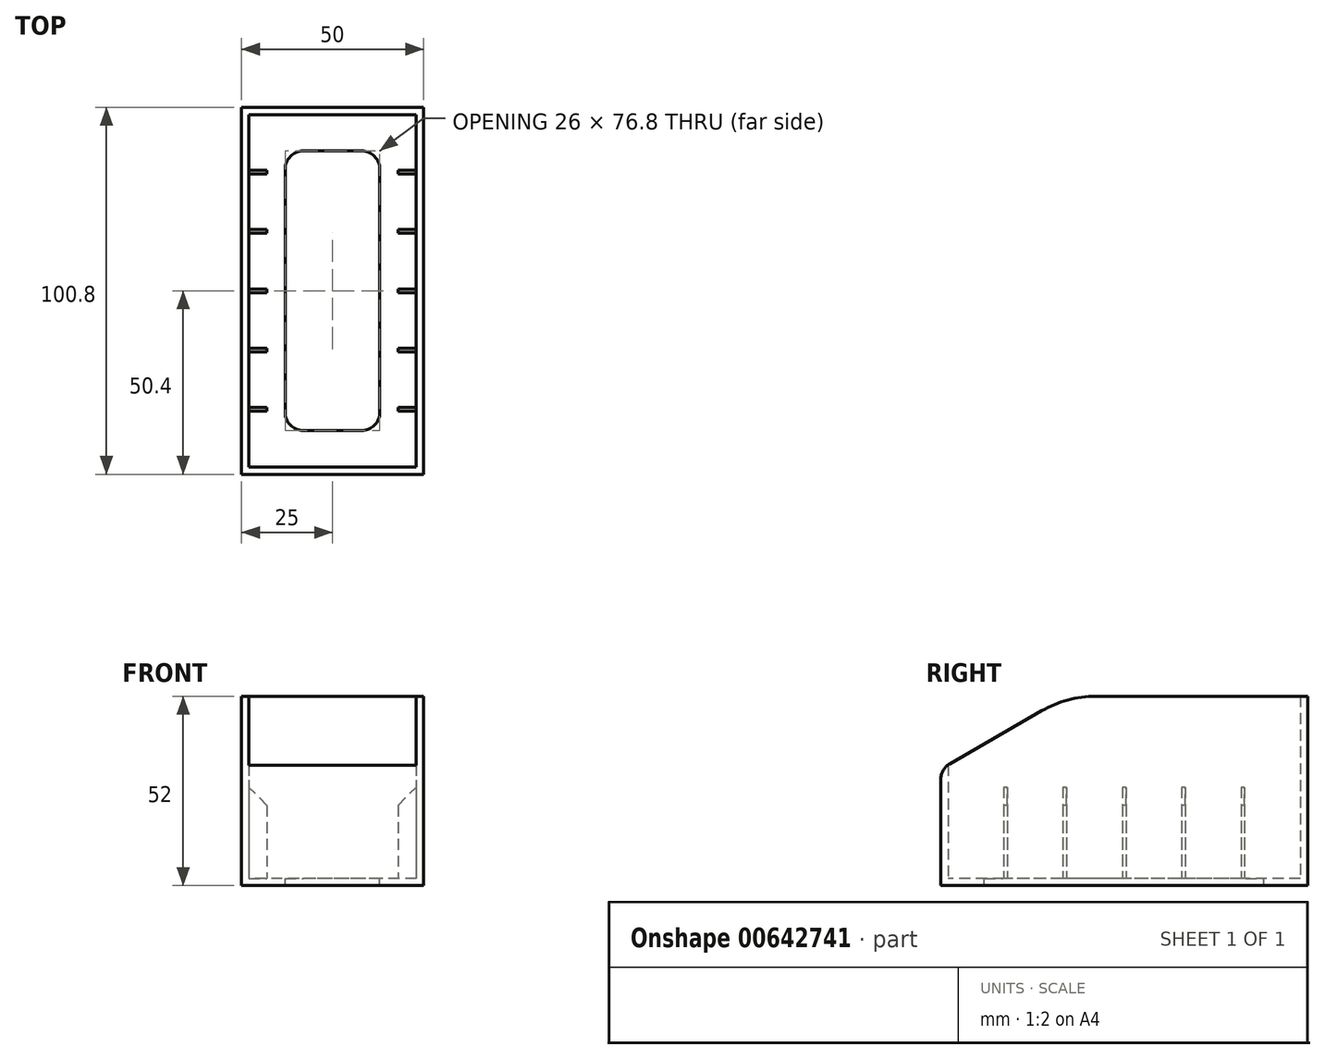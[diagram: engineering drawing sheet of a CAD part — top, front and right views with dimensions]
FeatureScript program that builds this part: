
annotation { "Feature Type Name" : "Feature", "Feature Type Description" : "" }
export const myFeature = defineFeature(function(context is Context, id is Id, definition is map)
    precondition{}
    {
        {
            var Q0;
            Q0=qCreatedBy(makeId("Top.planeOp"),FACE);
            var sketch = newSketch(context, id + "F0", { "sketchPlane" : qUnion([Q0])});
            skLineSegment(sketch, "E0.bottom", {"start": v(23, 48.4) * mm, "end": v(-23, 48.4) * mm});
            skLineSegment(sketch, "E0.top", {"start": v(23, -48.4) * mm, "end": v(-23, -48.4) * mm});
            skLineSegment(sketch, "E0.left", {"start": v(23, 48.4) * mm, "end": v(23, -48.4) * mm});
            skLineSegment(sketch, "E0.right", {"start": v(-23, 48.4) * mm, "end": v(-23, -48.4) * mm});
            skPoint(sketch, "E0.middle", {"position": v(0, 0) * mm});
            skLineSegment(sketch, "E1.bottom", {"start": v(25, 50.4) * mm, "end": v(-25, 50.4) * mm});
            skLineSegment(sketch, "E1.top", {"start": v(25, -50.4) * mm, "end": v(-25, -50.4) * mm});
            skLineSegment(sketch, "E1.left", {"start": v(25, 50.4) * mm, "end": v(25, -50.4) * mm});
            skLineSegment(sketch, "E1.right", {"start": v(-25, 50.4) * mm, "end": v(-25, -50.4) * mm});
            skSolve(sketch);
        }
        {
            var Q0;
            Q0 = qSketchRegion(id + "F0", true);
            extrude(context, id + "F1", {"entities" : qUnion([Q0]), "depth" : 50 * mm, "offsetDistance" : 25 * mm});
        }
        {
            var Q0;
            Q0=qCreatedBy(makeId("Top.planeOp"),FACE);
            var sketch = newSketch(context, id + "F2", { "sketchPlane" : qUnion([Q0])});
            skLineSegment(sketch, "E2.0", {"start": v(-25, 50.4) * mm, "end": v(-25, -50.4) * mm});
            skLineSegment(sketch, "E3.0", {"start": v(25, -50.4) * mm, "end": v(-25, -50.4) * mm});
            skLineSegment(sketch, "E4.0", {"start": v(25, 50.4) * mm, "end": v(25, -50.4) * mm});
            skLineSegment(sketch, "E5.0", {"start": v(25, 50.4) * mm, "end": v(-25, 50.4) * mm});
            skLineSegment(sketch, "E6.bottom", {"start": v(13, 38.4) * mm, "end": v(-13, 38.4) * mm});
            skLineSegment(sketch, "E6.top", {"start": v(13, -38.4) * mm, "end": v(-13, -38.4) * mm});
            skLineSegment(sketch, "E6.left", {"start": v(13, 38.4) * mm, "end": v(13, -38.4) * mm});
            skLineSegment(sketch, "E6.right", {"start": v(-13, 38.4) * mm, "end": v(-13, -38.4) * mm});
            skPoint(sketch, "E6.middle", {"position": v(0, 0) * mm});
            skSolve(sketch);
        }
        {
            var Q0;
            Q0=makeQuery(id+"F2.imprint","IMPRINT",FACE,{"disambiguationData":[TD([[makeQuery(id+"F2.imprint","IMPRINT",EDGE,{"derivedFrom":sQuery(id+"F2.wireOp",EDGE,"E2.0")}),1.0]])]});
            extrude(context, id + "F3", {"entities" : qUnion([Q0]), "operationType" : NewBodyOperationType.ADD, "oppositeDirection" : true, "depth" : 2 * mm, "offsetDistance" : 25 * mm});
        }
        {
            var Q0;
            Q0=makeQuery(id+"F1.opExtrude","CAP_EDGE",EDGE,{"disambiguationData":[OSD([sQuery(id+"F0.wireOp",EDGE,"E1.top")])],"isStart":false});
            chamfer(context, id + "F4", {"entities" : qUnion([Q0]), "chamferType" : ChamferType.OFFSET_ANGLE, "width" : 20 * mm, "oppositeDirection" : false, "angle" : 60 * degree, "tangentPropagation" : true});
        }
        {
            var Q0;
            {var subQ0=sQuery(id+"F0.wireOp",EDGE,"E1.top");Q0=makeQuery(id+"F4.opChamfer","BLEND_EDGE",EDGE,{"disambiguationData":[OD(1.0)],"blendedFrom":[makeQuery(id+"F1.opExtrude","CAP_EDGE",EDGE,{"disambiguationData":[OSD([subQ0])],"isStart":false}),makeQuery(id+"F1.opExtrude","CAP_FACE",FACE,{"disambiguationData":[OSD([sQuery(id+"F0.wireOp",EDGE,"E0.bottom"),sQuery(id+"F0.wireOp",EDGE,"E0.top"),sQuery(id+"F0.wireOp",EDGE,"E0.left"),sQuery(id+"F0.wireOp",EDGE,"E0.right"),sQuery(id+"F0.wireOp",EDGE,"E1.bottom"),subQ0,sQuery(id+"F0.wireOp",EDGE,"E1.left"),sQuery(id+"F0.wireOp",EDGE,"E1.right")])],"isStart":false})],"blendedInto":[makeQuery(id+"F1.opExtrude","CAP_FACE",FACE,{"disambiguationData":[OSD([sQuery(id+"F0.wireOp",EDGE,"E0.bottom"),sQuery(id+"F0.wireOp",EDGE,"E0.top"),sQuery(id+"F0.wireOp",EDGE,"E0.left"),sQuery(id+"F0.wireOp",EDGE,"E0.right"),sQuery(id+"F0.wireOp",EDGE,"E1.bottom"),subQ0,sQuery(id+"F0.wireOp",EDGE,"E1.left"),sQuery(id+"F0.wireOp",EDGE,"E1.right")])],"isStart":false})]});}
            var Q1;
            {var subQ0=sQuery(id+"F0.wireOp",EDGE,"E1.top");Q1=makeQuery(id+"F4.opChamfer","BLEND_EDGE",EDGE,{"disambiguationData":[OD(0.0)],"blendedFrom":[makeQuery(id+"F1.opExtrude","CAP_EDGE",EDGE,{"disambiguationData":[OSD([subQ0])],"isStart":false}),makeQuery(id+"F1.opExtrude","CAP_FACE",FACE,{"disambiguationData":[OSD([sQuery(id+"F0.wireOp",EDGE,"E0.bottom"),sQuery(id+"F0.wireOp",EDGE,"E0.top"),sQuery(id+"F0.wireOp",EDGE,"E0.left"),sQuery(id+"F0.wireOp",EDGE,"E0.right"),sQuery(id+"F0.wireOp",EDGE,"E1.bottom"),subQ0,sQuery(id+"F0.wireOp",EDGE,"E1.left"),sQuery(id+"F0.wireOp",EDGE,"E1.right")])],"isStart":false})],"blendedInto":[makeQuery(id+"F1.opExtrude","CAP_FACE",FACE,{"disambiguationData":[OSD([sQuery(id+"F0.wireOp",EDGE,"E0.bottom"),sQuery(id+"F0.wireOp",EDGE,"E0.top"),sQuery(id+"F0.wireOp",EDGE,"E0.left"),sQuery(id+"F0.wireOp",EDGE,"E0.right"),sQuery(id+"F0.wireOp",EDGE,"E1.bottom"),subQ0,sQuery(id+"F0.wireOp",EDGE,"E1.left"),sQuery(id+"F0.wireOp",EDGE,"E1.right")])],"isStart":false})]});}
            fillet(context, id + "F5", {"entities" : qUnion([Q0, Q1]), "radius" : 30 * mm, "tangentPropagation" : true, "allowEdgeOverflow" : false});
        }
        {
            var Q0;
            {var subQ0=sQuery(id+"F0.wireOp",EDGE,"E1.top");Q0=makeQuery(id+"F4.opChamfer","BLEND_EDGE",EDGE,{"blendedFrom":[makeQuery(id+"F1.opExtrude","CAP_EDGE",EDGE,{"disambiguationData":[OSD([subQ0])],"isStart":false}),makeQuery(id+"F3.boolean.opBoolean","MERGE",FACE,{"derivedFrom":[makeQuery(id+"F1.opExtrude","SWEPT_FACE",FACE,{"disambiguationData":[OSD([subQ0])]}),makeQuery(id+"F3.opExtrude","SWEPT_FACE",FACE,{"disambiguationData":[OSD([sQuery(id+"F2.wireOp",EDGE,"E3.0")])]})]})],"blendedInto":[makeQuery(id+"F3.boolean.opBoolean","MERGE",FACE,{"derivedFrom":[makeQuery(id+"F1.opExtrude","SWEPT_FACE",FACE,{"disambiguationData":[OSD([subQ0])]}),makeQuery(id+"F3.opExtrude","SWEPT_FACE",FACE,{"disambiguationData":[OSD([sQuery(id+"F2.wireOp",EDGE,"E3.0")])]})]})]});}
            fillet(context, id + "F6", {"entities" : qUnion([Q0]), "radius" : 5 * mm, "tangentPropagation" : true, "allowEdgeOverflow" : false});
        }
        {
            var Q0;
            Q0=makeQuery(id+"F3.opExtrude","SWEPT_EDGE",EDGE,{"disambiguationData":[OSD([sQuery(id+"F2.wireOp",EDGE,"E6.bottom"),sQuery(id+"F2.wireOp",EDGE,"E6.left")])]});
            var Q1;
            Q1=makeQuery(id+"F3.opExtrude","SWEPT_EDGE",EDGE,{"disambiguationData":[OSD([sQuery(id+"F2.wireOp",EDGE,"E6.bottom"),sQuery(id+"F2.wireOp",EDGE,"E6.right")])]});
            var Q2;
            Q2=makeQuery(id+"F3.opExtrude","SWEPT_EDGE",EDGE,{"disambiguationData":[OSD([sQuery(id+"F2.wireOp",EDGE,"E6.top"),sQuery(id+"F2.wireOp",EDGE,"E6.left")])]});
            var Q3;
            Q3=makeQuery(id+"F3.opExtrude","SWEPT_EDGE",EDGE,{"disambiguationData":[OSD([sQuery(id+"F2.wireOp",EDGE,"E6.top"),sQuery(id+"F2.wireOp",EDGE,"E6.right")])]});
            fillet(context, id + "F7", {"entities" : qUnion([Q0, Q1, Q2, Q3]), "radius" : 5 * mm, "tangentPropagation" : true, "allowEdgeOverflow" : false});
        }
        {
            var Q0;
            Q0=makeQuery(id+"F3.opExtrude","CAP_FACE",FACE,{"disambiguationData":[OSD([sQuery(id+"F2.wireOp",EDGE,"E2.0"),sQuery(id+"F2.wireOp",EDGE,"E3.0"),sQuery(id+"F2.wireOp",EDGE,"E4.0"),sQuery(id+"F2.wireOp",EDGE,"E5.0"),sQuery(id+"F2.wireOp",EDGE,"E6.bottom"),sQuery(id+"F2.wireOp",EDGE,"E6.top"),sQuery(id+"F2.wireOp",EDGE,"E6.left"),sQuery(id+"F2.wireOp",EDGE,"E6.right")])],"isStart":true});
            var sketch = newSketch(context, id + "F8", { "sketchPlane" : qUnion([Q0])});
            skLineSegment(sketch, "E7.bottom", {"start": v(-23, 33.1) * mm, "end": v(-18, 33.1) * mm});
            skLineSegment(sketch, "E7.top", {"start": v(-23, 32.1) * mm, "end": v(-18, 32.1) * mm});
            skLineSegment(sketch, "E7.left", {"start": v(-23, 33.1) * mm, "end": v(-23, 32.1) * mm});
            skLineSegment(sketch, "E7.right", {"start": v(-18, 33.1) * mm, "end": v(-18, 32.1) * mm});
            skLineSegment(sketch, "E8.bottom", {"start": v(-23, 16.8) * mm, "end": v(-18, 16.8) * mm});
            skLineSegment(sketch, "E8.top", {"start": v(-23, 15.8) * mm, "end": v(-18, 15.8) * mm});
            skLineSegment(sketch, "E8.left", {"start": v(-23, 16.8) * mm, "end": v(-23, 15.8) * mm});
            skLineSegment(sketch, "E8.right", {"start": v(-18, 16.8) * mm, "end": v(-18, 15.8) * mm});
            skLineSegment(sketch, "E9.bottom", {"start": v(-23, 0.5) * mm, "end": v(-18, 0.5) * mm});
            skLineSegment(sketch, "E9.top", {"start": v(-23, -0.5) * mm, "end": v(-18, -0.5) * mm});
            skLineSegment(sketch, "E9.left", {"start": v(-23, 0.5) * mm, "end": v(-23, -0.5) * mm});
            skLineSegment(sketch, "E9.right", {"start": v(-18, 0.5) * mm, "end": v(-18, -0.5) * mm});
            skLineSegment(sketch, "E10.bottom", {"start": v(-23, -15.8) * mm, "end": v(-18, -15.8) * mm});
            skLineSegment(sketch, "E10.top", {"start": v(-23, -16.8) * mm, "end": v(-18, -16.8) * mm});
            skLineSegment(sketch, "E10.left", {"start": v(-23, -15.8) * mm, "end": v(-23, -16.8) * mm});
            skLineSegment(sketch, "E10.right", {"start": v(-18, -15.8) * mm, "end": v(-18, -16.8) * mm});
            skLineSegment(sketch, "E11.bottom", {"start": v(-23, -32.1) * mm, "end": v(-18, -32.1) * mm});
            skLineSegment(sketch, "E11.top", {"start": v(-23, -33.1) * mm, "end": v(-18, -33.1) * mm});
            skLineSegment(sketch, "E11.left", {"start": v(-23, -32.1) * mm, "end": v(-23, -33.1) * mm});
            skLineSegment(sketch, "E11.right", {"start": v(-18, -32.1) * mm, "end": v(-18, -33.1) * mm});
            skLineSegment(sketch, "E12.MirrorCS", {"start": v(18, 33.1) * mm, "end": v(18, 32.1) * mm});
            skLineSegment(sketch, "E13.MirrorCS", {"start": v(18, -32.1) * mm, "end": v(18, -33.1) * mm});
            skLineSegment(sketch, "E14.MirrorCS", {"start": v(18, -15.8) * mm, "end": v(18, -16.8) * mm});
            skLineSegment(sketch, "E15.MirrorCS", {"start": v(23, 33.1) * mm, "end": v(23, 32.1) * mm});
            skLineSegment(sketch, "E16.MirrorCS", {"start": v(23, 16.8) * mm, "end": v(23, 15.8) * mm});
            skLineSegment(sketch, "E17.MirrorCS", {"start": v(23, -15.8) * mm, "end": v(23, -16.8) * mm});
            skLineSegment(sketch, "E18.MirrorCS", {"start": v(23, -32.1) * mm, "end": v(23, -33.1) * mm});
            skLineSegment(sketch, "E19.MirrorCS", {"start": v(23, 0.5) * mm, "end": v(23, -0.5) * mm});
            skLineSegment(sketch, "E20.MirrorCS", {"start": v(18, 0.5) * mm, "end": v(18, -0.5) * mm});
            skLineSegment(sketch, "E21.MirrorCS", {"start": v(18, 16.8) * mm, "end": v(18, 15.8) * mm});
            skLineSegment(sketch, "E22.MirrorCS", {"start": v(23, 16.8) * mm, "end": v(18, 16.8) * mm});
            skLineSegment(sketch, "E23.MirrorCS", {"start": v(23, 33.1) * mm, "end": v(18, 33.1) * mm});
            skLineSegment(sketch, "E24.MirrorCS", {"start": v(23, 32.1) * mm, "end": v(18, 32.1) * mm});
            skLineSegment(sketch, "E25.MirrorCS", {"start": v(23, 15.8) * mm, "end": v(18, 15.8) * mm});
            skLineSegment(sketch, "E26.MirrorCS", {"start": v(23, -16.8) * mm, "end": v(18, -16.8) * mm});
            skLineSegment(sketch, "E27.MirrorCS", {"start": v(23, -33.1) * mm, "end": v(18, -33.1) * mm});
            skLineSegment(sketch, "E28.MirrorCS", {"start": v(23, -32.1) * mm, "end": v(18, -32.1) * mm});
            skLineSegment(sketch, "E29.MirrorCS", {"start": v(23, -15.8) * mm, "end": v(18, -15.8) * mm});
            skLineSegment(sketch, "E30.MirrorCS", {"start": v(23, 0.5) * mm, "end": v(18, 0.5) * mm});
            skLineSegment(sketch, "E31.MirrorCS", {"start": v(23, -0.5) * mm, "end": v(18, -0.5) * mm});
            skSolve(sketch);
        }
        {
            var Q0;
            Q0=makeQuery(id+"F8.imprint","IMPRINT",FACE,{"disambiguationData":[TD([[makeQuery(id+"F8.imprint","IMPRINT",EDGE,{"derivedFrom":sQuery(id+"F8.wireOp",EDGE,"E7.bottom")}),-1.0]])]});
            var Q1;
            Q1=makeQuery(id+"F8.imprint","IMPRINT",FACE,{"disambiguationData":[TD([[makeQuery(id+"F8.imprint","IMPRINT",EDGE,{"derivedFrom":sQuery(id+"F8.wireOp",EDGE,"E8.bottom")}),-1.0]])]});
            var Q2;
            Q2=makeQuery(id+"F8.imprint","IMPRINT",FACE,{"disambiguationData":[TD([[makeQuery(id+"F8.imprint","IMPRINT",EDGE,{"derivedFrom":sQuery(id+"F8.wireOp",EDGE,"E9.bottom")}),-1.0]])]});
            var Q3;
            Q3=makeQuery(id+"F8.imprint","IMPRINT",FACE,{"disambiguationData":[TD([[makeQuery(id+"F8.imprint","IMPRINT",EDGE,{"derivedFrom":sQuery(id+"F8.wireOp",EDGE,"E10.bottom")}),-1.0]])]});
            var Q4;
            Q4=makeQuery(id+"F8.imprint","IMPRINT",FACE,{"disambiguationData":[TD([[makeQuery(id+"F8.imprint","IMPRINT",EDGE,{"derivedFrom":sQuery(id+"F8.wireOp",EDGE,"E11.bottom")}),-1.0]])]});
            var Q5;
            Q5=makeQuery(id+"F8.imprint","IMPRINT",FACE,{"disambiguationData":[TD([[makeQuery(id+"F8.imprint","IMPRINT",EDGE,{"derivedFrom":sQuery(id+"F8.wireOp",EDGE,"E13.MirrorCS")}),1.0]])]});
            var Q6;
            Q6=makeQuery(id+"F8.imprint","IMPRINT",FACE,{"disambiguationData":[TD([[makeQuery(id+"F8.imprint","IMPRINT",EDGE,{"derivedFrom":sQuery(id+"F8.wireOp",EDGE,"E14.MirrorCS")}),1.0]])]});
            var Q7;
            Q7=makeQuery(id+"F8.imprint","IMPRINT",FACE,{"disambiguationData":[TD([[makeQuery(id+"F8.imprint","IMPRINT",EDGE,{"derivedFrom":sQuery(id+"F8.wireOp",EDGE,"E16.MirrorCS")}),-1.0]])]});
            var Q8;
            Q8=makeQuery(id+"F8.imprint","IMPRINT",FACE,{"disambiguationData":[TD([[makeQuery(id+"F8.imprint","IMPRINT",EDGE,{"derivedFrom":sQuery(id+"F8.wireOp",EDGE,"E19.MirrorCS")}),-1.0]])]});
            var Q9;
            Q9=makeQuery(id+"F8.imprint","IMPRINT",FACE,{"disambiguationData":[TD([[makeQuery(id+"F8.imprint","IMPRINT",EDGE,{"derivedFrom":sQuery(id+"F8.wireOp",EDGE,"E12.MirrorCS")}),1.0]])]});
            extrude(context, id + "F9", {"entities" : qUnion([Q0, Q1, Q2, Q3, Q4, Q5, Q6, Q7, Q8, Q9]), "operationType" : NewBodyOperationType.ADD, "depth" : 25 * mm, "offsetDistance" : 25 * mm});
        }
        {
            var Q0;
            Q0=makeQuery(id+"F9.opExtrude","CAP_EDGE",EDGE,{"disambiguationData":[OSD([sQuery(id+"F8.wireOp",EDGE,"E7.right")])],"isStart":false});
            var Q1;
            Q1=makeQuery(id+"F9.opExtrude","CAP_EDGE",EDGE,{"disambiguationData":[OSD([sQuery(id+"F8.wireOp",EDGE,"E8.right")])],"isStart":false});
            var Q2;
            Q2=makeQuery(id+"F9.opExtrude","CAP_EDGE",EDGE,{"disambiguationData":[OSD([sQuery(id+"F8.wireOp",EDGE,"E9.right")])],"isStart":false});
            var Q3;
            Q3=makeQuery(id+"F9.opExtrude","CAP_EDGE",EDGE,{"disambiguationData":[OSD([sQuery(id+"F8.wireOp",EDGE,"E10.right")])],"isStart":false});
            var Q4;
            Q4=makeQuery(id+"F9.opExtrude","CAP_EDGE",EDGE,{"disambiguationData":[OSD([sQuery(id+"F8.wireOp",EDGE,"E11.right")])],"isStart":false});
            var Q5;
            Q5=makeQuery(id+"F9.opExtrude","CAP_EDGE",EDGE,{"disambiguationData":[OSD([sQuery(id+"F8.wireOp",EDGE,"E13.MirrorCS")])],"isStart":false});
            var Q6;
            Q6=makeQuery(id+"F9.opExtrude","CAP_EDGE",EDGE,{"disambiguationData":[OSD([sQuery(id+"F8.wireOp",EDGE,"E14.MirrorCS")])],"isStart":false});
            var Q7;
            Q7=makeQuery(id+"F9.opExtrude","CAP_EDGE",EDGE,{"disambiguationData":[OSD([sQuery(id+"F8.wireOp",EDGE,"E20.MirrorCS")])],"isStart":false});
            var Q8;
            Q8=makeQuery(id+"F9.opExtrude","CAP_EDGE",EDGE,{"disambiguationData":[OSD([sQuery(id+"F8.wireOp",EDGE,"E21.MirrorCS")])],"isStart":false});
            var Q9;
            Q9=makeQuery(id+"F9.opExtrude","CAP_EDGE",EDGE,{"disambiguationData":[OSD([sQuery(id+"F8.wireOp",EDGE,"E12.MirrorCS")])],"isStart":false});
            chamfer(context, id + "F10", {"entities" : qUnion([Q0, Q1, Q2, Q3, Q4, Q5, Q6, Q7, Q8, Q9]), "width" : 5 * mm, "tangentPropagation" : true});
        }
    });
